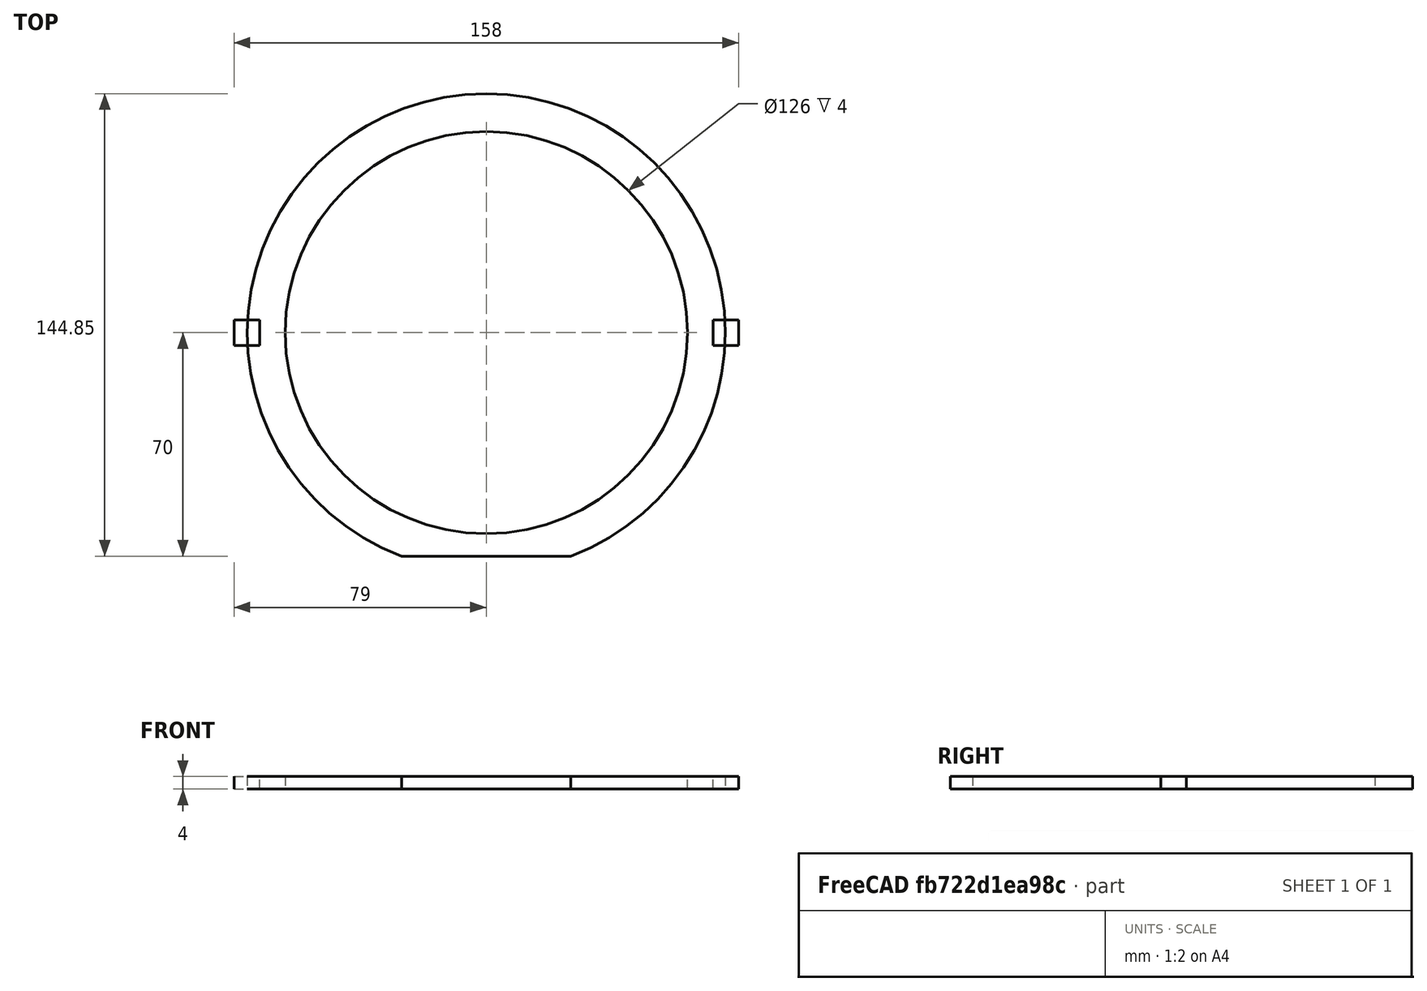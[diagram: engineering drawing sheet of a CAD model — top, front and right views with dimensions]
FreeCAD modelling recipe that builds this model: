
FCSTD DOCUMENT  (FreeCAD 0.19R0.19.2)
Label: waferHolder_002
License: All rights reserved
LicenseURL: http://en.wikipedia.org/wiki/All_rights_reserved
objects: Part::Box×2, Sketcher::SketchObject×1, Part::Extrusion×1
note: 4 computed .brp shape members not serialized (recipe doc carries the construction recipe); baked Part::Feature solids carry a one-line shape summary decoded from their .brp

FEATURE [Sketcher::SketchObject] Sketch
  FullyConstrained = true
  sketch-geometry (3):
    g0: Circle CenterX=-3.1415e-12 CenterY=5.6243e-12 CenterZ=0 NormalX=0 NormalY=0 NormalZ=1 AngleXU=0 Radius=63
    g1: ArcOfCircle CenterX=-3.1415e-12 CenterY=5.6243e-12 CenterZ=0 NormalX=0 NormalY=0 NormalZ=1 AngleXU=0 Radius=74.8482 StartAngle=5.07429 EndAngle=10.6337
    g2: LineSegment StartX=-26.5 StartY=-70.0001 StartZ=0 EndX=26.5 EndY=-70.0001 EndZ=0
  constraints (6):
    c: Block(g0)
    c: Coincident(g1,g0)
    c: Block(g1)
    c: Coincident(g2,g1)
    c: Coincident(g2,g1)
    c: Horizontal(g2)
FEATURE [Part::Box] Box  label="holderBitLeft"
  AttacherType = Attacher::AttachEngine3D
  Height = 4
  Length = 8
  Placement = pos=(-79,-4,0) rot=(0,0,1;0rad)
  Width = 8
FEATURE [Part::Box] Box001  label="holderBitRight"
  AttacherType = Attacher::AttachEngine3D
  Height = 4
  Length = 8
  Placement = pos=(71,-4,0) rot=(0,0,1;0rad)
  Width = 8
FEATURE [Part::Extrusion] Extrude
  Base = -> Sketch
  Dir = (0,0,1)
  DirMode = 2
  FaceMakerClass = Part::FaceMakerBullseye
  LengthFwd = 4
  LengthRev = 0
  Solid = true
  Symmetric = false
